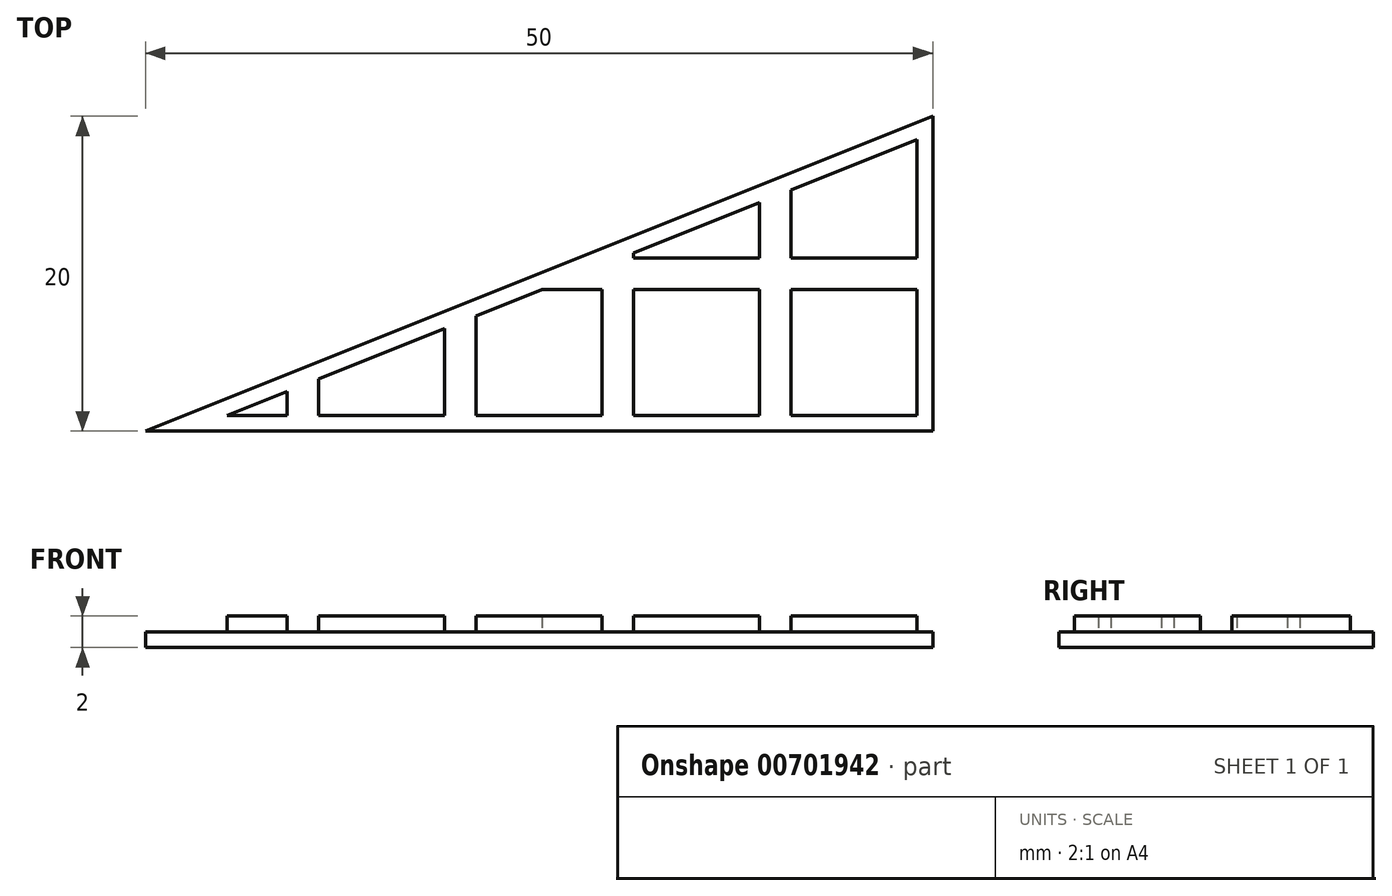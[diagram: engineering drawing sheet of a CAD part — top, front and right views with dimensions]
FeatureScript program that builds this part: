
annotation { "Feature Type Name" : "Feature", "Feature Type Description" : "" }
export const myFeature = defineFeature(function(context is Context, id is Id, definition is map)
    precondition{}
    {
        {
            var Q0;
            Q0=qCreatedBy(makeId("Top.planeOp"),FACE);
            var sketch = newSketch(context, id + "F0", { "sketchPlane" : qUnion([Q0])});
            skLineSegment(sketch, "E0", {"start": v(-50, 0) * mm, "end": v(0, 0) * mm});
            skLineSegment(sketch, "E1", {"start": v(0, 0) * mm, "end": v(0, 20) * mm});
            skLineSegment(sketch, "E2", {"start": v(0, 20) * mm, "end": v(-50, 0) * mm});
            skSolve(sketch);
        }
        {
            var Q0;
            Q0=makeQuery(id+"F0.imprint","IMPRINT",FACE,{"disambiguationData":[TD([[makeQuery(id+"F0.imprint","IMPRINT",EDGE,{"derivedFrom":sQuery(id+"F0.wireOp",EDGE,"qFyTJhzL-X8oy-V4Zn-n2UO-jb0vi0Htoton")}),1.0]])]});
            var Q1;
            Q1=makeQuery(id+"F0.imprint","IMPRINT",FACE,{"disambiguationData":[TD([[makeQuery(id+"F0.imprint","IMPRINT",EDGE,{"derivedFrom":sQuery(id+"F0.wireOp",EDGE,"8X8TdU3l-BQ1k-w8db-zCfl-hLHWanO2PYAS")}),1.0]])]});
            var Q2;
            Q2=makeQuery(id+"F0.imprint","IMPRINT",FACE,{"disambiguationData":[TD([[makeQuery(id+"F0.imprint","IMPRINT",EDGE,{"derivedFrom":sQuery(id+"F0.wireOp",EDGE,"WSVu92h9-HOxL-UAjn-v7h9-4ASb6rVnE2tI")}),1.0]])]});
            var Q3;
            Q3=makeQuery(id+"F0.imprint","IMPRINT",FACE,{"disambiguationData":[TD([[makeQuery(id+"F0.imprint","IMPRINT",EDGE,{"derivedFrom":sQuery(id+"F0.wireOp",EDGE,"E0")}),1.0]])]});
            extrude(context, id + "F1", {"entities" : qUnion([Q0, Q1, Q2, Q3]), "depth" : 1 * mm, "offsetDistance" : 25 * mm});
        }
        {
            var Q0;
            Q0=makeQuery(id+"F1.opExtrude","CAP_FACE",FACE,{"disambiguationData":[OSD([sQuery(id+"F0.wireOp",EDGE,"E0"),sQuery(id+"F0.wireOp",EDGE,"E1"),sQuery(id+"F0.wireOp",EDGE,"E2")])],"isStart":false});
            var sketch = newSketch(context, id + "F2", { "sketchPlane" : qUnion([Q0])});
            skLineSegment(sketch, "E3", {"start": v(-10, 16) * mm, "end": v(-10, 0) * mm, "construction": true});
            skLineSegment(sketch, "E4", {"start": v(-20, 12) * mm, "end": v(-20, 0) * mm, "construction": true});
            skLineSegment(sketch, "E5", {"start": v(-30, 8) * mm, "end": v(-30, 0) * mm, "construction": true});
            skLineSegment(sketch, "E6", {"start": v(-44.8, 1) * mm, "end": v(-1, 1) * mm});
            skLineSegment(sketch, "E7", {"start": v(-1, 1) * mm, "end": v(-1, 18.52) * mm});
            skLineSegment(sketch, "E8", {"start": v(-44.8, 1) * mm, "end": v(-1, 18.52) * mm});
            skLineSegment(sketch, "E9", {"start": v(-40, 2.92) * mm, "end": v(-40, 1) * mm, "construction": true});
            skLineSegment(sketch, "E10", {"start": v(-1, 10) * mm, "end": v(-22.3, 10) * mm, "construction": true});
            skLineSegment(sketch, "E11", {"start": v(-41, 2.52) * mm, "end": v(-41, 1) * mm});
            skLineSegment(sketch, "E12", {"start": v(-39, 3.32) * mm, "end": v(-39, 1) * mm});
            skLineSegment(sketch, "E13", {"start": v(-31, 6.52) * mm, "end": v(-31, 1) * mm});
            skLineSegment(sketch, "E14", {"start": v(-29, 7.32) * mm, "end": v(-29, 1) * mm});
            skLineSegment(sketch, "E15", {"start": v(-21, 10.52) * mm, "end": v(-21, 1) * mm});
            skLineSegment(sketch, "E16", {"start": v(-19, 11.32) * mm, "end": v(-19, 1) * mm});
            skLineSegment(sketch, "E17", {"start": v(-11, 14.52) * mm, "end": v(-11, 1) * mm});
            skLineSegment(sketch, "E18", {"start": v(-9, 15.32) * mm, "end": v(-9, 1) * mm});
            skLineSegment(sketch, "E19", {"start": v(-1, 11) * mm, "end": v(-19.8, 11) * mm});
            skLineSegment(sketch, "E20", {"start": v(-1, 9) * mm, "end": v(-24.8, 9) * mm});
            skSolve(sketch);
        }
        {
            var Q0;
            {var subQ0=sQuery(id+"F2.wireOp",EDGE,"E16");var subQ1=sQuery(id+"F2.wireOp",EDGE,"E8");var subQ2=makeQuery(id+"F2.imprint","INTERSECT",VERTEX,{"derivedFrom":[subQ1,subQ0]});Q0=makeQuery(id+"F2.imprint","IMPRINT",FACE,{"disambiguationData":[TD([[makeQuery(id+"F2.imprint","IMPRINT",EDGE,{"disambiguationData":[TD([[subQ2,-1.0]])],"derivedFrom":subQ1}),-1.0]])]});}
            var Q1;
            {var subQ5=sQuery(id+"F2.wireOp",EDGE,"E14");Q1=makeQuery(id+"F2.imprint","IMPRINT",FACE,{"disambiguationData":[TD([[makeQuery(id+"F2.imprint","IMPRINT",EDGE,{"derivedFrom":subQ5}),1.0]])]});}
            var Q2;
            {var subQ0=sQuery(id+"F2.wireOp",EDGE,"E12");Q2=makeQuery(id+"F2.imprint","IMPRINT",FACE,{"disambiguationData":[TD([[makeQuery(id+"F2.imprint","IMPRINT",EDGE,{"derivedFrom":subQ0}),1.0]])]});}
            var Q3;
            {var subQ0=sQuery(id+"F2.wireOp",EDGE,"E8");var subQ1=sQuery(id+"F2.wireOp",EDGE,"E7");var subQ2=makeQuery(id+"F2.imprint","INTERSECT",VERTEX,{"derivedFrom":[subQ1,subQ0]});Q3=makeQuery(id+"F2.imprint","IMPRINT",FACE,{"disambiguationData":[TD([[makeQuery(id+"F2.imprint","IMPRINT",EDGE,{"disambiguationData":[TD([[subQ2,1.0]])],"derivedFrom":subQ1}),1.0]])]});}
            var Q4;
            {var subQ0=sQuery(id+"F2.wireOp",EDGE,"E7");var subQ1=sQuery(id+"F2.wireOp",EDGE,"E6");var subQ2=makeQuery(id+"F2.imprint","INTERSECT",VERTEX,{"derivedFrom":[subQ1,subQ0]});Q4=makeQuery(id+"F2.imprint","IMPRINT",FACE,{"disambiguationData":[TD([[makeQuery(id+"F2.imprint","IMPRINT",EDGE,{"disambiguationData":[TD([[subQ2,1.0]])],"derivedFrom":subQ1}),1.0]])]});}
            var Q5;
            {var subQ0=sQuery(id+"F2.wireOp",EDGE,"E16");var subQ1=sQuery(id+"F2.wireOp",EDGE,"E6");var subQ2=makeQuery(id+"F2.imprint","INTERSECT",VERTEX,{"derivedFrom":[subQ1,subQ0]});Q5=makeQuery(id+"F2.imprint","IMPRINT",FACE,{"disambiguationData":[TD([[makeQuery(id+"F2.imprint","IMPRINT",EDGE,{"disambiguationData":[TD([[subQ2,-1.0]])],"derivedFrom":subQ1}),1.0]])]});}
            var Q6;
            {var subQ3=sQuery(id+"F2.wireOp",EDGE,"E11");Q6=makeQuery(id+"F2.imprint","IMPRINT",FACE,{"disambiguationData":[TD([[makeQuery(id+"F2.imprint","IMPRINT",EDGE,{"derivedFrom":subQ3}),-1.0]])]});}
            extrude(context, id + "F3", {"entities" : qUnion([Q0, Q1, Q2, Q3, Q4, Q5, Q6]), "operationType" : NewBodyOperationType.ADD, "depth" : 1 * mm, "offsetDistance" : 25 * mm});
        }
    });
